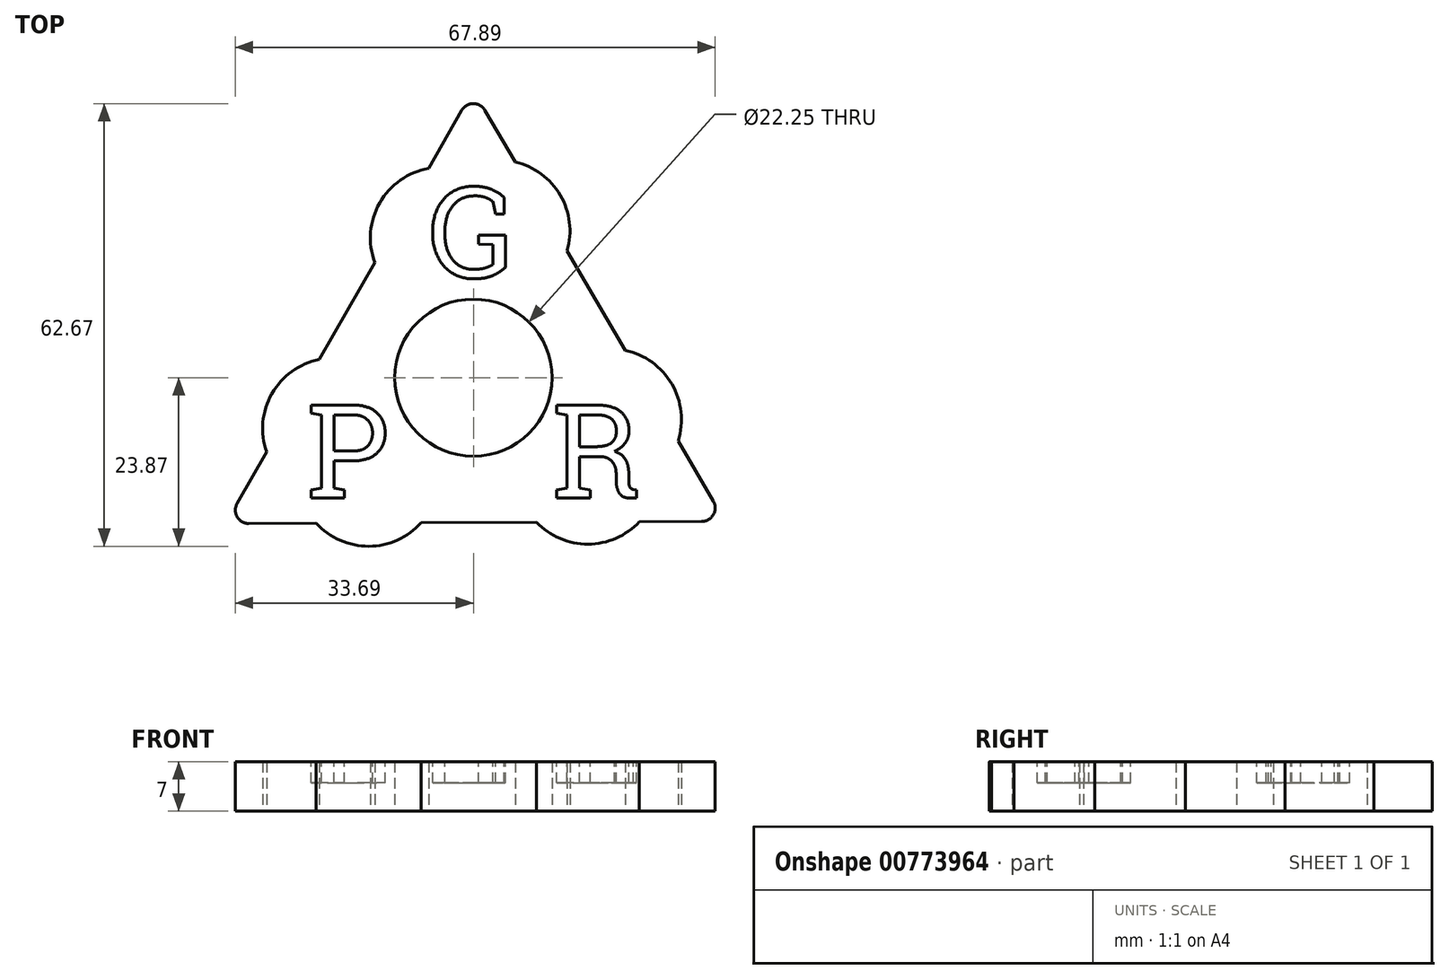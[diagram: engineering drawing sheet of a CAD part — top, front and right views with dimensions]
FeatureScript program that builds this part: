
annotation { "Feature Type Name" : "Feature", "Feature Type Description" : "" }
export const myFeature = defineFeature(function(context is Context, id is Id, definition is map)
    precondition{}
    {
        {
            var Q0;
            Q0=qCreatedBy(makeId("Top.planeOp"),FACE);
            var sketch = newSketch(context, id + "F0", { "sketchPlane" : qUnion([Q0])});
            skCircle(sketch, "E0", {"center": v(0, 0) * mm, "radius": 11.12 * mm});
            skLineSegment(sketch, "E1.0", {"start": v(-35.07, -20.67) * mm, "end": v(-0.02, 40.7) * mm});
            skLineSegment(sketch, "E1.1", {"start": v(-0.02, 40.7) * mm, "end": v(35.6, -20.33) * mm});
            skLineSegment(sketch, "E1.2", {"start": v(35.6, -20.33) * mm, "end": v(-35.07, -20.67) * mm});
            skPoint(sketch, "E1.0.midPoint", {"position": v(-17.55, 10.02) * mm});
            skArc(sketch, "E2", {"start": v(-6.34, 29.64) * mm, "mid": v(-13.27, 24.75) * mm, "end": v(-13.96, 16.3) * mm});
            skArc(sketch, "E3", {"start": v(-21.8, 2.58) * mm, "mid": v(-28.52, -2.27) * mm, "end": v(-29.27, -10.52) * mm});
            skArc(sketch, "E4.1.0", {"start": v(-22.5, -20.31) * mm, "mid": v(-14.8, -23.87) * mm, "end": v(-7.14, -20.24) * mm});
            skArc(sketch, "E4.1.1", {"start": v(8.67, -20.16) * mm, "mid": v(16.22, -23.56) * mm, "end": v(23.75, -20.1) * mm});
            skArc(sketch, "E4.2.0", {"start": v(28.84, -9.32) * mm, "mid": v(28.07, -0.89) * mm, "end": v(21.1, 3.93) * mm});
            skArc(sketch, "E4.2.1", {"start": v(13.13, 17.59) * mm, "mid": v(12.3, 25.83) * mm, "end": v(5.53, 30.61) * mm});
            skSolve(sketch);
        }
        {
            var Q0;
            Q0=qSketchRegion(id+"F0",true);
            extrude(context, id + "F1", {"entities" : qUnion([Q0]), "depth" : 7 * mm, "offsetDistance" : 25 * mm});
        }
        {
            var Q0;
            Q0=makeQuery(id+"F1.opExtrude","CAP_FACE",FACE,{"disambiguationData":[OSD([sQuery(id+"F0.wireOp",EDGE,"E0"),sQuery(id+"F0.wireOp",EDGE,"E1.0"),sQuery(id+"F0.wireOp",EDGE,"E1.1"),sQuery(id+"F0.wireOp",EDGE,"E1.2")])],"isStart":false});
            var sketch = newSketch(context, id + "F2", { "sketchPlane" : qUnion([Q0])});
            skText(sketch, "E5", { "text": "G", "fontName": "RobotoSlab-Regular.ttf"});
            skText(sketch, "E6", { "text": "P     R\n", "fontName": "RobotoSlab-Regular.ttf"});
            const initialGuessF2  = {"E5": [-0.00625, 0.01418, 1, 0, 0.0129], "E6": [-0.02363, -0.01704, 1, 0, 0.01333]};
            skSetInitialGuess(sketch, initialGuessF2);
            skSolve(sketch);
        }
        {
            var Q0;
            Q0=qSketchRegion(id+"F2",true);
            extrude(context, id + "F3", {"entities" : qUnion([Q0]), "operationType" : NewBodyOperationType.REMOVE, "oppositeDirection" : true, "depth" : 3 * mm, "offsetDistance" : 25 * mm});
        }
        {
            var Q0;
            Q0=makeQuery(id+"F1.opExtrude","SWEPT_EDGE",EDGE,{"disambiguationData":[OSD([sQuery(id+"F0.wireOp",EDGE,"E1.0"),sQuery(id+"F0.wireOp",EDGE,"E1.2")])]});
            var Q1;
            Q1=makeQuery(id+"F1.opExtrude","SWEPT_EDGE",EDGE,{"disambiguationData":[OSD([sQuery(id+"F0.wireOp",EDGE,"E1.0"),sQuery(id+"F0.wireOp",EDGE,"E1.1")])]});
            var Q2;
            Q2=makeQuery(id+"F1.opExtrude","SWEPT_EDGE",EDGE,{"disambiguationData":[OSD([sQuery(id+"F0.wireOp",EDGE,"E1.1"),sQuery(id+"F0.wireOp",EDGE,"E1.2")])]});
            fillet(context, id + "F4", {"entities" : qUnion([Q0, Q1, Q2]), "radius" : 1.9 * mm, "tangentPropagation" : true, "allowEdgeOverflow" : false});
        }
    });
